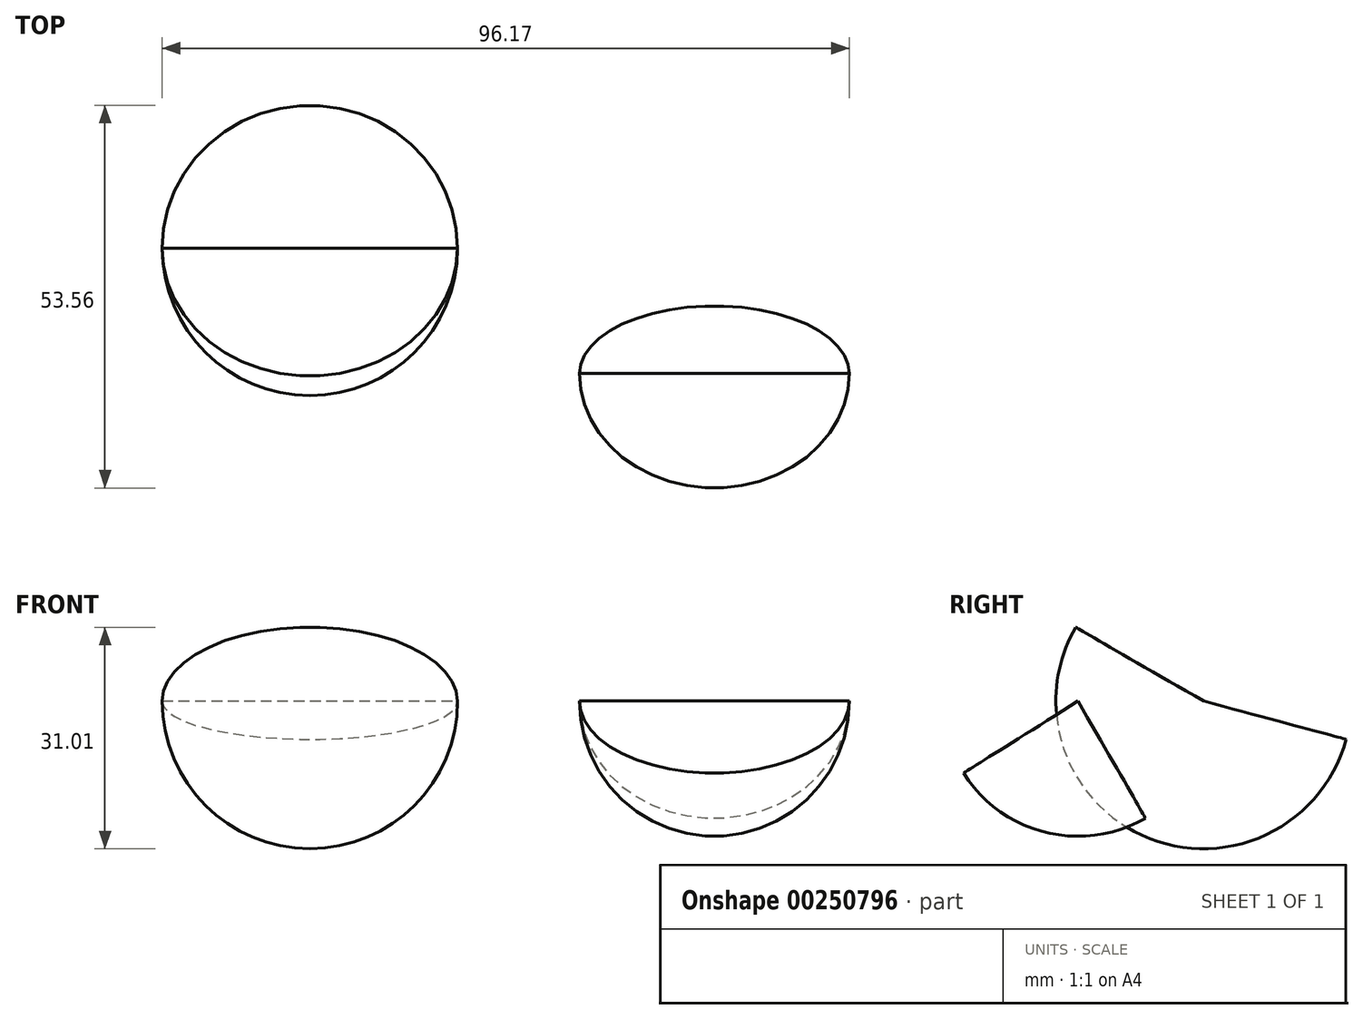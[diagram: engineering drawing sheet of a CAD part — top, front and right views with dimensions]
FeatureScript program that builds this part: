
annotation { "Feature Type Name" : "Feature", "Feature Type Description" : "" }
export const myFeature = defineFeature(function(context is Context, id is Id, definition is map)
    precondition{}
    {
        {
            var Q0;
            Q0=qCreatedBy(makeId("Top.planeOp"),FACE);
            var sketch = newSketch(context, id + "F0", { "sketchPlane" : qUnion([Q0])});
            skArc(sketch, "E0", {"start": v(0, 0) * mm, "mid": v(18.87, -18.92) * mm, "end": v(37.75, 0) * mm});
            skLineSegment(sketch, "E1", {"start": v(0, 0) * mm, "end": v(37.75, 0) * mm});
            skCircle(sketch, "E2", {"center": v(-37.75, 17.57) * mm, "radius": 20.67 * mm});
            skLineSegment(sketch, "E3", {"start": v(-58.42, 17.57) * mm, "end": v(-17.07, 17.57) * mm});
            skSolve(sketch);
        }
        {
            var Q0;
            Q0=makeQuery(id+"F0.imprint","IMPRINT",FACE,{"disambiguationData":[TD([[makeQuery(id+"F0.imprint","IMPRINT",EDGE,{"derivedFrom":sQuery(id+"F0.wireOp",EDGE,"E0")}),1.0]])]});
            var Q1;
            Q1=sQuery(id+"F0.wireOp",EDGE,"E1");
            revolve(context, id + "F1", {"entities" : qUnion([Q0]), "axis" : qUnion([Q1]), "revolveType" : RevolveType.TWO_DIRECTIONS, "angle" : 120 * degree, "angleBack" : 32.16 * degree});
        }
        {
            var Q0;
            {var subQ0=sQuery(id+"F0.wireOp",EDGE,"E3");Q0=makeQuery(id+"F0.imprint","IMPRINT",FACE,{"disambiguationData":[TD([[makeQuery(id+"F0.imprint","IMPRINT",EDGE,{"derivedFrom":subQ0}),-1.0]])]});}
            var Q1;
            Q1=sQuery(id+"F0.wireOp",EDGE,"E3");
            revolve(context, id + "F2", {"entities" : qUnion([Q0]), "axis" : qUnion([Q1]), "revolveType" : RevolveType.TWO_DIRECTIONS, "angle" : 165 * degree, "angleBack" : 330 * degree});
        }
    });
